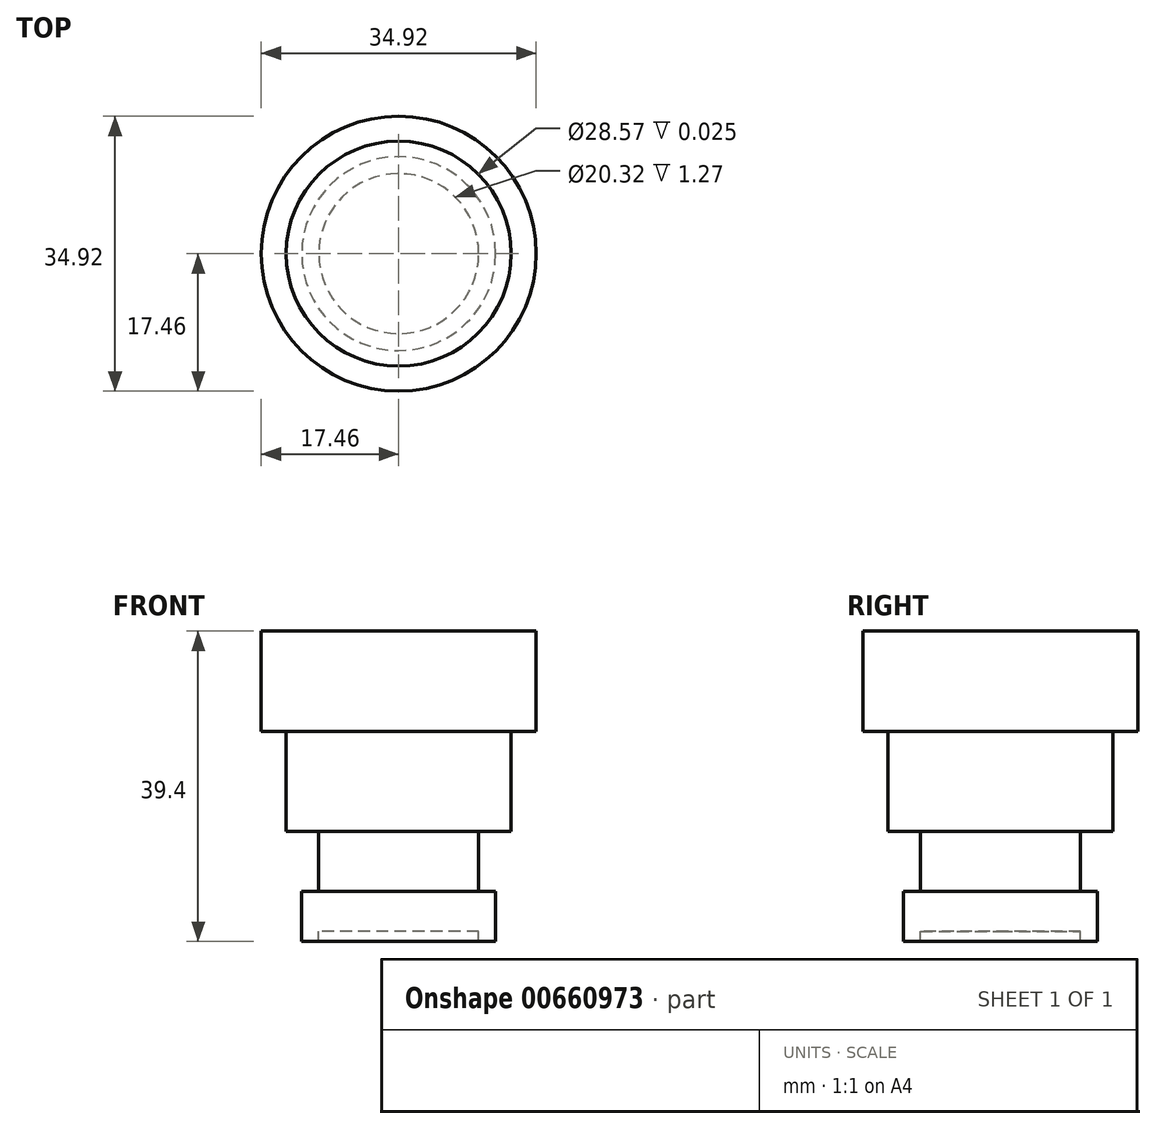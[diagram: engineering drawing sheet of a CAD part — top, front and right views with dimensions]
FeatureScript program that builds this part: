
annotation { "Feature Type Name" : "Feature", "Feature Type Description" : "" }
export const myFeature = defineFeature(function(context is Context, id is Id, definition is map)
    precondition{}
    {
        {
            var Q0;
            Q0=qCreatedBy(makeId("Top.planeOp"),FACE);
            var sketch = newSketch(context, id + "F0", { "sketchPlane" : qUnion([Q0])});
            skCircle(sketch, "E0", {"center": v(0, 0) * mm, "radius": 14.29 * mm});
            skCircle(sketch, "E1.0", {"center": v(0, 0) * mm, "radius": 17.46 * mm});
            skCircle(sketch, "E2", {"center": v(0, 0) * mm, "radius": 12.32 * mm});
            skCircle(sketch, "E3", {"center": v(0, 0) * mm, "radius": 10.16 * mm});
            skSolve(sketch);
        }
        {
            var Q0;
            Q0=makeQuery(id+"F0.imprint","IMPRINT",FACE,{"disambiguationData":[TD([[makeQuery(id+"F0.imprint","IMPRINT",EDGE,{"derivedFrom":sQuery(id+"F0.wireOp",EDGE,"E0")}),1.0]])]});
            var Q1;
            Q1=makeQuery(id+"F0.imprint","IMPRINT",FACE,{"disambiguationData":[TD([[makeQuery(id+"F0.imprint","IMPRINT",EDGE,{"derivedFrom":sQuery(id+"F0.wireOp",EDGE,"E3")}),1.0]])]});
            var Q2;
            Q2=makeQuery(id+"F0.imprint","IMPRINT",FACE,{"disambiguationData":[TD([[makeQuery(id+"F0.imprint","IMPRINT",EDGE,{"derivedFrom":sQuery(id+"F0.wireOp",EDGE,"E2")}),1.0]])]});
            extrude(context, id + "F1", {"entities" : qUnion([Q0, Q1, Q2]), "oppositeDirection" : true, "depth" : 25.43 * mm, "offsetDistance" : 25.4 * mm});
        }
        {
            var Q0;
            Q0=qSketchRegion(id+"F0",true);
            extrude(context, id + "F2", {"entities" : qUnion([Q0]), "operationType" : NewBodyOperationType.ADD, "oppositeDirection" : true, "depth" : 12.7 * mm, "offsetDistance" : 25.4 * mm, "hasSecondDirection" : true, "secondDirectionOppositeDirection" : false, "secondDirectionDepth" : 0.03 * mm});
        }
        {
            var Q0;
            Q0=makeQuery(id+"F0.imprint","IMPRINT",FACE,{"disambiguationData":[TD([[makeQuery(id+"F0.imprint","IMPRINT",EDGE,{"derivedFrom":sQuery(id+"F0.wireOp",EDGE,"E3")}),1.0]])]});
            extrude(context, id + "F3", {"entities" : qUnion([Q0]), "operationType" : NewBodyOperationType.ADD, "oppositeDirection" : true, "depth" : 38.1 * mm, "offsetDistance" : 25.4 * mm, "hasSecondDirection" : true, "secondDirectionOppositeDirection" : true, "secondDirectionDepth" : 25.4 * mm});
        }
        {
            var Q0;
            Q0=makeQuery(id+"F0.imprint","IMPRINT",FACE,{"disambiguationData":[TD([[makeQuery(id+"F0.imprint","IMPRINT",EDGE,{"derivedFrom":sQuery(id+"F0.wireOp",EDGE,"E2")}),1.0]])]});
            extrude(context, id + "F4", {"entities" : qUnion([Q0]), "operationType" : NewBodyOperationType.ADD, "oppositeDirection" : true, "depth" : 39.37 * mm, "offsetDistance" : 25.4 * mm, "hasSecondDirection" : true, "secondDirectionOppositeDirection" : true, "secondDirectionDepth" : 33.02 * mm});
        }
    });
